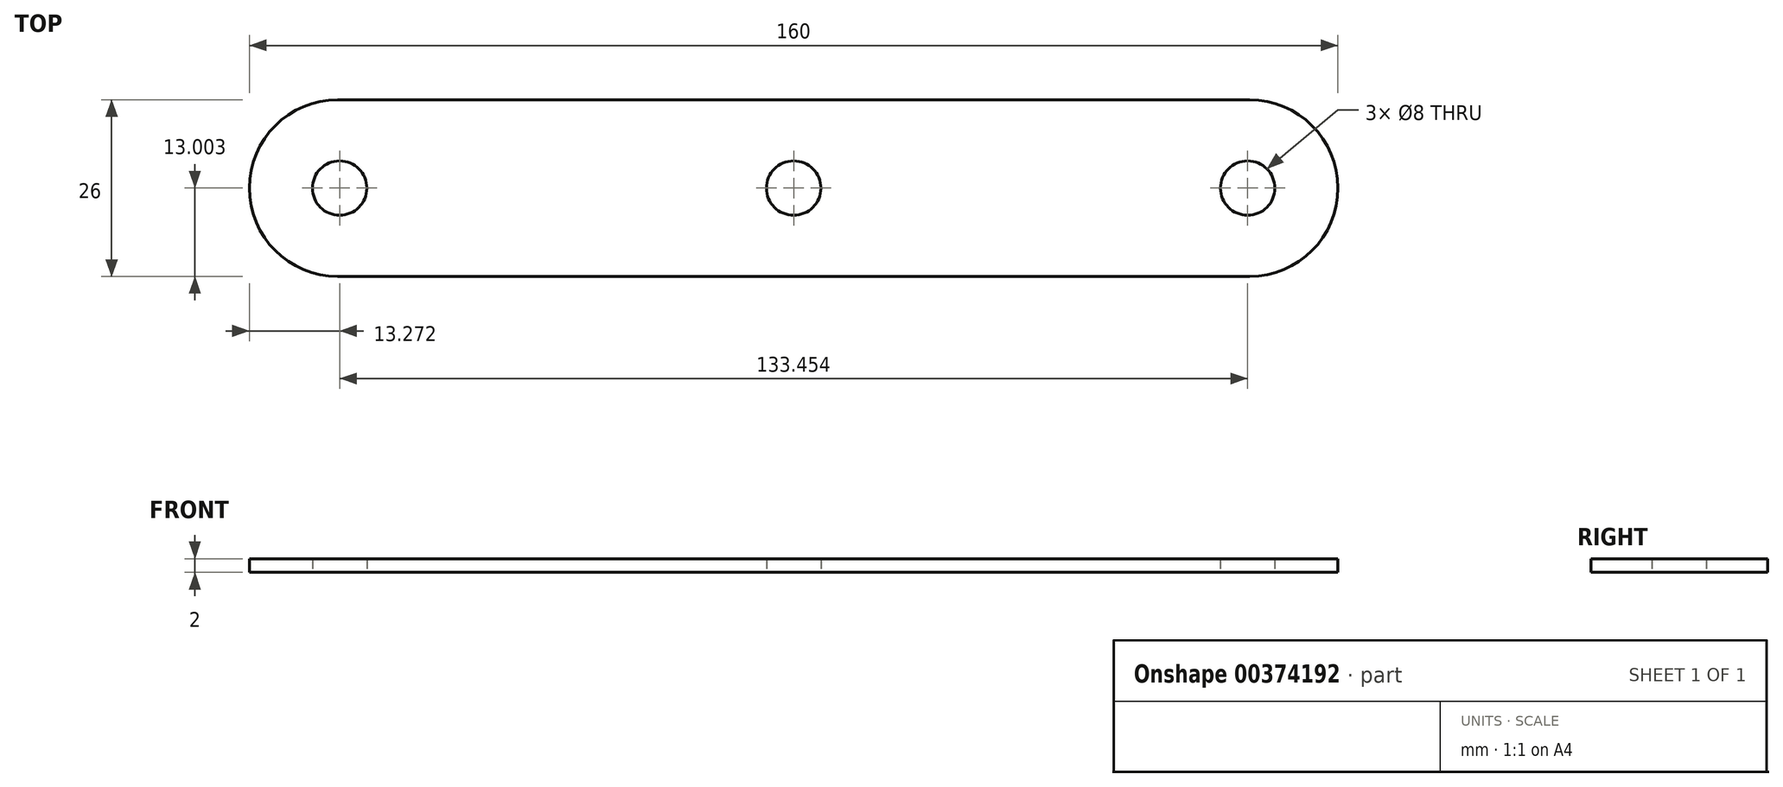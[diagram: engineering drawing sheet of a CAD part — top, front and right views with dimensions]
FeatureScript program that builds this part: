
annotation { "Feature Type Name" : "Feature", "Feature Type Description" : "" }
export const myFeature = defineFeature(function(context is Context, id is Id, definition is map)
    precondition{}
    {
        {
            var Q0;
            Q0=qCreatedBy(makeId("Top.planeOp"),FACE);
            var sketch = newSketch(context, id + "F0", { "sketchPlane" : qUnion([Q0])});
            skLineSegment(sketch, "E0.bottom", {"start": v(-61.9, 4.53) * mm, "end": v(72.1, 4.53) * mm});
            skLineSegment(sketch, "E0.top", {"start": v(-61.9, -21.47) * mm, "end": v(72.1, -21.47) * mm});
            skLineSegment(sketch, "E0.left", {"start": v(-74.9, -8.47) * mm, "end": v(-74.9, -8.47) * mm});
            skLineSegment(sketch, "E0.right", {"start": v(85.1, -8.47) * mm, "end": v(85.1, -8.47) * mm});
            skLineSegment(sketch, "E1", {"start": v(-74.9, -8.47) * mm, "end": v(85.1, -8.47) * mm, "construction": true});
            skLineSegment(sketch, "E2", {"start": v(5.1, -8.47) * mm, "end": v(5.1, 4.53) * mm, "construction": true});
            skLineSegment(sketch, "E3", {"start": v(5.1, -8.47) * mm, "end": v(5.1, -21.47) * mm, "construction": true});
            skCircle(sketch, "E4", {"center": v(-61.63, -8.47) * mm, "radius": 4 * mm});
            skLineSegment(sketch, "E5", {"start": v(-65.4, -7.14) * mm, "end": v(-74.9, -7.14) * mm, "construction": true});
            skLineSegment(sketch, "E6", {"start": v(-61.63, -8.47) * mm, "end": v(-61.63, 4.53) * mm, "construction": true});
            skCircle(sketch, "E7.MirrorC", {"center": v(71.83, -8.47) * mm, "radius": 4 * mm});
            skCircle(sketch, "E8", {"center": v(5.1, -8.47) * mm, "radius": 4 * mm});
            skPoint(sketch, "E9.visualSharp", {"position": v(-74.9, -21.47) * mm});
            skArc(sketch, "E9.filletArc", {"start": v(-74.9, -8.47) * mm, "mid": v(-71.1, -17.66) * mm, "end": v(-61.9, -21.47) * mm});
            skPoint(sketch, "E10.visualSharp", {"position": v(-74.9, 4.53) * mm});
            skArc(sketch, "E10.filletArc", {"start": v(-61.9, 4.53) * mm, "mid": v(-71.1, 0.73) * mm, "end": v(-74.9, -8.47) * mm});
            skPoint(sketch, "E11.visualSharp", {"position": v(85.1, 4.53) * mm});
            skArc(sketch, "E11.filletArc", {"start": v(85.1, -8.47) * mm, "mid": v(81.3, 0.73) * mm, "end": v(72.1, 4.53) * mm});
            skPoint(sketch, "E12.visualSharp", {"position": v(85.1, -21.47) * mm});
            skArc(sketch, "E12.filletArc", {"start": v(72.1, -21.47) * mm, "mid": v(81.3, -17.66) * mm, "end": v(85.1, -8.47) * mm});
            skSolve(sketch);
        }
        {
            var Q0;
            Q0=makeQuery(id+"F0.imprint","IMPRINT",FACE,{"disambiguationData":[TD([[makeQuery(id+"F0.imprint","IMPRINT",EDGE,{"derivedFrom":sQuery(id+"F0.wireOp",EDGE,"E0.bottom")}),-1.0]])]});
            extrude(context, id + "F1", {"entities" : qUnion([Q0]), "depth" : 2 * mm});
        }
    });
